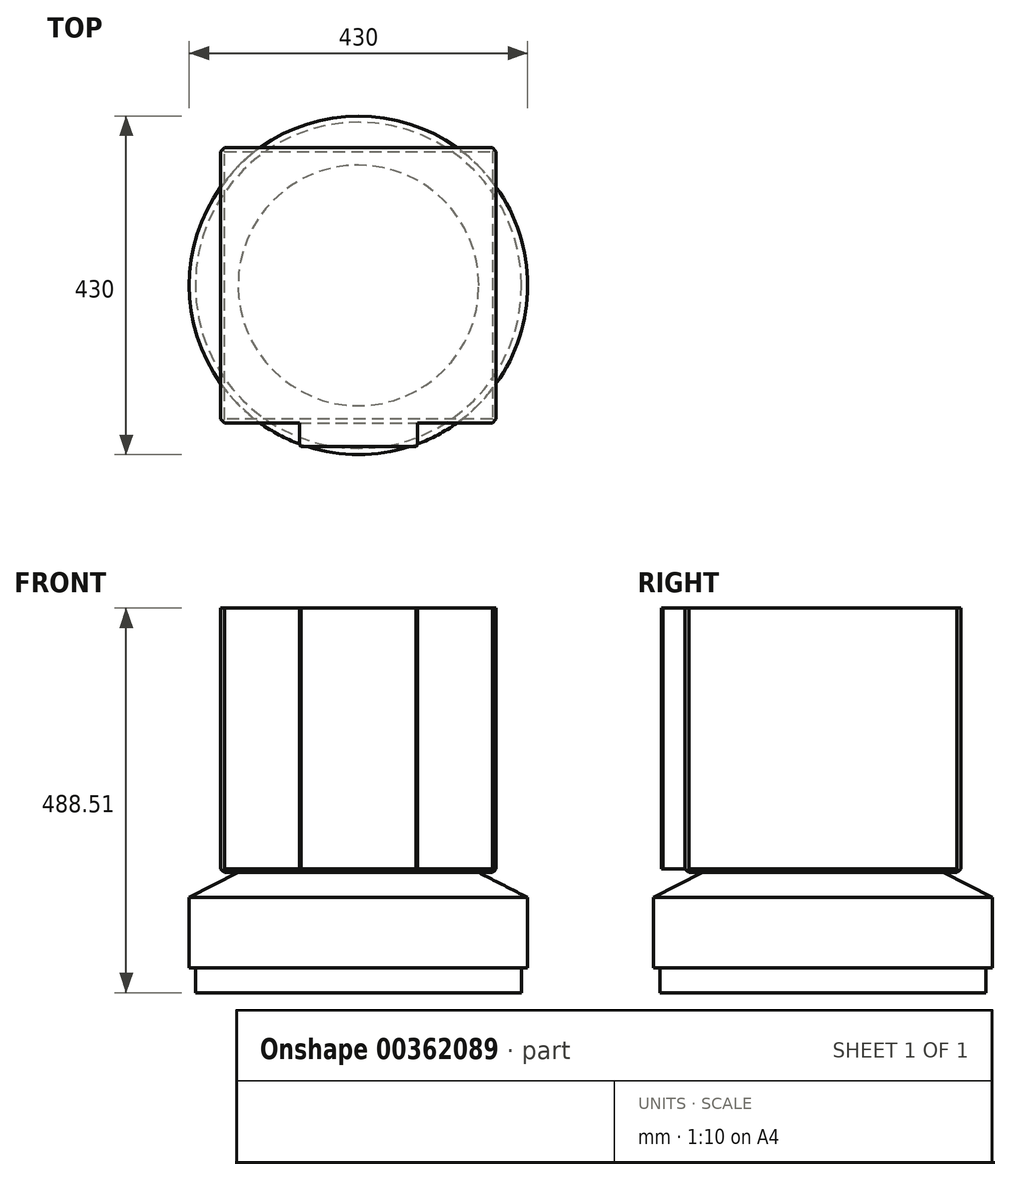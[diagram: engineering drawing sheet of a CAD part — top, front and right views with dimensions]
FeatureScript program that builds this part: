
annotation { "Feature Type Name" : "Feature", "Feature Type Description" : "" }
export const myFeature = defineFeature(function(context is Context, id is Id, definition is map)
    precondition{}
    {
        {
            var Q0;
            Q0=qCreatedBy(makeId("Front.planeOp"),FACE);
            var sketch = newSketch(context, id + "F0", { "sketchPlane" : qUnion([Q0])});
            skLineSegment(sketch, "E0", {"start": v(-166.1, -120.82) * mm, "end": v(41.05, -120.82) * mm});
            skPoint(sketch, "E0.startSnap0", {"position": v(224.91, -120.82) * mm});
            skLineSegment(sketch, "E1", {"start": v(-166.1, -89.02) * mm, "end": v(-166.1, -120.82) * mm});
            skLineSegment(sketch, "E2", {"start": v(-166.1, -89.02) * mm, "end": v(41.05, -89.02) * mm});
            skLineSegment(sketch, "E3", {"start": v(-166.1, -89.02) * mm, "end": v(-173.95, -89.02) * mm});
            skLineSegment(sketch, "E4", {"start": v(-173.95, -89.02) * mm, "end": v(-173.95, 0) * mm});
            skLineSegment(sketch, "E5", {"start": v(-173.95, 0) * mm, "end": v(41.05, 0) * mm});
            skLineSegment(sketch, "E6", {"start": v(-173.95, -34.06) * mm, "end": v(41.05, -34.06) * mm});
            skLineSegment(sketch, "E7", {"start": v(-173.95, 0) * mm, "end": v(-91.55, 42.05) * mm});
            skLineSegment(sketch, "E8", {"start": v(-91.55, 42.05) * mm, "end": v(41.05, 42.05) * mm});
            skLineSegment(sketch, "E9", {"start": v(41.05, 171.5) * mm, "end": v(41.05, -194.52) * mm});
            skPoint(sketch, "E10.orphan", {"position": v(249.25, 0) * mm});
            skPoint(sketch, "E11.trimOffspring.end.orphan", {"position": v(249.25, -34.06) * mm});
            skPoint(sketch, "E12.orphan", {"position": v(249.25, -89.02) * mm});
            skPoint(sketch, "E13.start.orphan", {"position": v(224.91, -97.66) * mm});
            skPoint(sketch, "E14.end.orphan", {"position": v(224.91, -143.99) * mm});
            skLineSegment(sketch, "E15.MirrorCS", {"start": v(173.64, 42.05) * mm, "end": v(41.05, 42.05) * mm});
            skLineSegment(sketch, "E16.MirrorCS", {"start": v(256.05, 0) * mm, "end": v(173.64, 42.05) * mm});
            skLineSegment(sketch, "E17.MirrorCS", {"start": v(256.05, -89.02) * mm, "end": v(256.05, 0) * mm});
            skLineSegment(sketch, "E18.MirrorCS", {"start": v(256.05, 0) * mm, "end": v(41.05, 0) * mm});
            skLineSegment(sketch, "E19.MirrorCS", {"start": v(256.05, -34.06) * mm, "end": v(41.05, -34.06) * mm});
            skLineSegment(sketch, "E20.MirrorCS", {"start": v(248.2, -89.02) * mm, "end": v(41.05, -89.02) * mm});
            skLineSegment(sketch, "E21", {"start": v(184.14, -89.02) * mm, "end": v(184.14, -120.82) * mm});
            skLineSegment(sketch, "E22.trimOffspring", {"start": v(184.14, -120.82) * mm, "end": v(41.05, -120.82) * mm});
            skPoint(sketch, "E23.MirrorCS.start.orphan", {"position": v(248.2, -120.82) * mm});
            skPoint(sketch, "E24.MirrorCS.start.orphan", {"position": v(248.2, -89.02) * mm});
            skLineSegment(sketch, "E25", {"start": v(184.14, -89.02) * mm, "end": v(256.05, -89.02) * mm});
            skLineSegment(sketch, "E26", {"start": v(41.05, 171.5) * mm, "end": v(41.05, 367.69) * mm});
            skPoint(sketch, "E27.end.orphan", {"position": v(80.24, 367.69) * mm});
            skLineSegment(sketch, "E28", {"start": v(41.05, 367.69) * mm, "end": v(-133.95, 367.69) * mm});
            skLineSegment(sketch, "E29", {"start": v(-133.95, 367.69) * mm, "end": v(-133.95, 42.05) * mm});
            skLineSegment(sketch, "E30", {"start": v(-91.55, 42.05) * mm, "end": v(-133.95, 42.05) * mm});
            skSolve(sketch);
        }
        {
            var Q0;
            {var subQ2=sQuery(id+"F0.wireOp",EDGE,"E8");Q0=makeQuery(id+"F0.imprint","IMPRINT",FACE,{"disambiguationData":[TD([[makeQuery(id+"F0.imprint","IMPRINT",EDGE,{"derivedFrom":subQ2}),1.0]])]});}
            var Q1;
            Q1=makeQuery(id+"F0.imprint","IMPRINT",FACE,{"disambiguationData":[TD([[makeQuery(id+"F0.imprint","IMPRINT",EDGE,{"derivedFrom":sQuery(id+"F0.wireOp",EDGE,"E7")}),-1.0]])]});
            var Q2;
            {var subQ2=sQuery(id+"F0.wireOp",EDGE,"E6");Q2=makeQuery(id+"F0.imprint","IMPRINT",FACE,{"disambiguationData":[TD([[makeQuery(id+"F0.imprint","IMPRINT",EDGE,{"derivedFrom":subQ2}),1.0]])]});}
            var Q3;
            {var subQ3=sQuery(id+"F0.wireOp",EDGE,"E2");Q3=makeQuery(id+"F0.imprint","IMPRINT",FACE,{"disambiguationData":[TD([[makeQuery(id+"F0.imprint","IMPRINT",EDGE,{"derivedFrom":subQ3}),1.0]])]});}
            var Q4;
            {var subQ0=sQuery(id+"F0.wireOp",EDGE,"E0");Q4=makeQuery(id+"F0.imprint","IMPRINT",FACE,{"disambiguationData":[TD([[makeQuery(id+"F0.imprint","IMPRINT",EDGE,{"derivedFrom":subQ0}),1.0]])]});}
            var Q5;
            Q5=sQuery(id+"F0.wireOp",EDGE,"E9");
            revolve(context, id + "F1", {"entities" : qUnion([Q0, Q1, Q2, Q3, Q4]), "axis" : qUnion([Q5]), "revolveType" : RevolveType.FULL});
        }
        {
            var Q0;
            Q0=makeQuery(id+"F1.opRevolve","SWEPT_FACE",FACE,{"disambiguationData":[OSD([sQuery(id+"F0.wireOp",EDGE,"E28")])]});
            var sketch = newSketch(context, id + "F2", { "sketchPlane" : qUnion([Q0])});
            skLineSegment(sketch, "E31.bottom", {"start": v(-133.95, 175) * mm, "end": v(216.05, 175) * mm});
            skLineSegment(sketch, "E31.top", {"start": v(-133.95, -175) * mm, "end": v(216.05, -175) * mm});
            skLineSegment(sketch, "E31.left", {"start": v(-133.95, 175) * mm, "end": v(-133.95, -175) * mm});
            skLineSegment(sketch, "E31.right", {"start": v(216.05, 175) * mm, "end": v(216.05, -175) * mm});
            skSolve(sketch);
        }
        {
            var Q0;
            {var subQ0=sQuery(id+"F2.wireOp",EDGE,"E31.left");var subQ1=sQuery(id+"F2.wireOp",EDGE,"E31.bottom");var subQ2=makeQuery(id+"F2.imprint","INTERSECT",VERTEX,{"derivedFrom":[subQ1,subQ0]});Q0=makeQuery(id+"F2.imprint","IMPRINT",FACE,{"disambiguationData":[TD([[makeQuery(id+"F2.imprint","IMPRINT",EDGE,{"disambiguationData":[TD([[subQ2,-1.0]])],"derivedFrom":subQ1}),-1.0]])]});}
            var Q1;
            {var subQ0=makeQuery(id+"F1.opRevolve","SWEPT_EDGE",EDGE,{"disambiguationData":[OSD([sQuery(id+"F0.wireOp",EDGE,"E28"),sQuery(id+"F0.wireOp",EDGE,"E29")])]});var subQ1=makeQuery(id+"F2.imprint","INTERSECT",VERTEX,{"derivedFrom":[subQ0,sQuery(id+"F2.wireOp",EDGE,"E31.bottom")]});Q1=makeQuery(id+"F2.imprint","IMPRINT",FACE,{"disambiguationData":[TD([[makeQuery(id+"F2.imprint","IMPRINT",EDGE,{"disambiguationData":[TD([[subQ1,-1.0]])],"derivedFrom":subQ0}),1.0]])]});}
            var Q2;
            {var subQ0=sQuery(id+"F2.wireOp",EDGE,"E31.right");var subQ1=sQuery(id+"F2.wireOp",EDGE,"E31.bottom");var subQ2=makeQuery(id+"F2.imprint","INTERSECT",VERTEX,{"derivedFrom":[subQ1,subQ0]});Q2=makeQuery(id+"F2.imprint","IMPRINT",FACE,{"disambiguationData":[TD([[makeQuery(id+"F2.imprint","IMPRINT",EDGE,{"disambiguationData":[TD([[subQ2,1.0]])],"derivedFrom":subQ1}),-1.0]])]});}
            var Q3;
            {var subQ0=sQuery(id+"F2.wireOp",EDGE,"E31.right");var subQ1=sQuery(id+"F2.wireOp",EDGE,"E31.top");var subQ2=makeQuery(id+"F2.imprint","INTERSECT",VERTEX,{"derivedFrom":[subQ1,subQ0]});Q3=makeQuery(id+"F2.imprint","IMPRINT",FACE,{"disambiguationData":[TD([[makeQuery(id+"F2.imprint","IMPRINT",EDGE,{"disambiguationData":[TD([[subQ2,1.0]])],"derivedFrom":subQ1}),1.0]])]});}
            var Q4;
            {var subQ0=sQuery(id+"F2.wireOp",EDGE,"E31.left");var subQ1=sQuery(id+"F2.wireOp",EDGE,"E31.top");var subQ2=makeQuery(id+"F2.imprint","INTERSECT",VERTEX,{"derivedFrom":[subQ1,subQ0]});Q4=makeQuery(id+"F2.imprint","IMPRINT",FACE,{"disambiguationData":[TD([[makeQuery(id+"F2.imprint","IMPRINT",EDGE,{"disambiguationData":[TD([[subQ2,-1.0]])],"derivedFrom":subQ1}),1.0]])]});}
            extrude(context, id + "F3", {"entities" : qUnion([Q0, Q1, Q2, Q3, Q4]), "operationType" : NewBodyOperationType.ADD, "oppositeDirection" : true, "depth" : 336 * mm});
        }
        {
            var Q0;
            Q0=makeQuery(id+"F3.opExtrude","CAP_EDGE",EDGE,{"disambiguationData":[OSD([sQuery(id+"F2.wireOp",EDGE,"E31.bottom")])],"isStart":false});
            var Q1;
            Q1=makeQuery(id+"F3.opExtrude","CAP_EDGE",EDGE,{"disambiguationData":[OSD([sQuery(id+"F2.wireOp",EDGE,"E31.left")])],"isStart":false});
            var Q2;
            Q2=makeQuery(id+"F3.opExtrude","CAP_EDGE",EDGE,{"disambiguationData":[OSD([sQuery(id+"F2.wireOp",EDGE,"E31.right")])],"isStart":false});
            var Q3;
            Q3=makeQuery(id+"F3.opExtrude","CAP_EDGE",EDGE,{"disambiguationData":[OSD([sQuery(id+"F2.wireOp",EDGE,"E31.top")])],"isStart":false});
            chamfer(context, id + "F4", {"entities" : qUnion([Q0, Q1, Q2, Q3]), "width" : 5 * mm, "tangentPropagation" : true});
        }
        {
            var Q0;
            Q0=makeQuery(id+"F3.opExtrude","SWEPT_EDGE",EDGE,{"disambiguationData":[OSD([sQuery(id+"F2.wireOp",EDGE,"E31.bottom"),sQuery(id+"F2.wireOp",EDGE,"E31.right")])]});
            var Q1;
            Q1=makeQuery(id+"F3.opExtrude","SWEPT_EDGE",EDGE,{"disambiguationData":[OSD([sQuery(id+"F2.wireOp",EDGE,"E31.top"),sQuery(id+"F2.wireOp",EDGE,"E31.right")])]});
            var Q2;
            Q2=makeQuery(id+"F3.opExtrude","SWEPT_EDGE",EDGE,{"disambiguationData":[OSD([sQuery(id+"F2.wireOp",EDGE,"E31.bottom"),sQuery(id+"F2.wireOp",EDGE,"E31.left")])]});
            var Q3;
            Q3=makeQuery(id+"F3.opExtrude","SWEPT_EDGE",EDGE,{"disambiguationData":[OSD([sQuery(id+"F2.wireOp",EDGE,"E31.top"),sQuery(id+"F2.wireOp",EDGE,"E31.left")])]});
            chamfer(context, id + "F5", {"entities" : qUnion([Q0, Q1, Q2, Q3]), "width" : 5 * mm, "tangentPropagation" : true});
        }
        {
            var Q0;
            Q0=makeQuery(id+"F3.opExtrude","SWEPT_FACE",FACE,{"disambiguationData":[OSD([sQuery(id+"F2.wireOp",EDGE,"E31.top")])]});
            var sketch = newSketch(context, id + "F6", { "sketchPlane" : qUnion([Q0])});
            skLineSegment(sketch, "E32", {"start": v(-33.95, 36.69) * mm, "end": v(-33.95, 367.69) * mm});
            skLineSegment(sketch, "E33", {"start": v(116.05, 367.69) * mm, "end": v(116.05, 36.69) * mm});
            skLineSegment(sketch, "E34", {"start": v(-33.95, 36.69) * mm, "end": v(116.05, 36.69) * mm});
            skLineSegment(sketch, "E35", {"start": v(-33.95, 367.69) * mm, "end": v(116.05, 367.69) * mm});
            skSolve(sketch);
        }
        {
            var Q0;
            Q0=makeQuery(id+"F6.imprint","IMPRINT",FACE,{"disambiguationData":[TD([[makeQuery(id+"F6.imprint","IMPRINT",EDGE,{"derivedFrom":sQuery(id+"F6.wireOp",EDGE,"E32")}),-1.0]])]});
            extrude(context, id + "F7", {"entities" : qUnion([Q0]), "operationType" : NewBodyOperationType.ADD, "depth" : 30 * mm});
        }
        {
            var Q0;
            Q0=makeQuery(id+"F7.opExtrude","CAP_EDGE",EDGE,{"disambiguationData":[OSD([sQuery(id+"F6.wireOp",EDGE,"E32")])],"isStart":false});
            var Q1;
            Q1=makeQuery(id+"F7.opExtrude","CAP_EDGE",EDGE,{"disambiguationData":[OSD([sQuery(id+"F6.wireOp",EDGE,"E33")])],"isStart":false});
            chamfer(context, id + "F8", {"entities" : qUnion([Q0, Q1]), "width" : 2 * mm, "tangentPropagation" : true});
        }
    });
